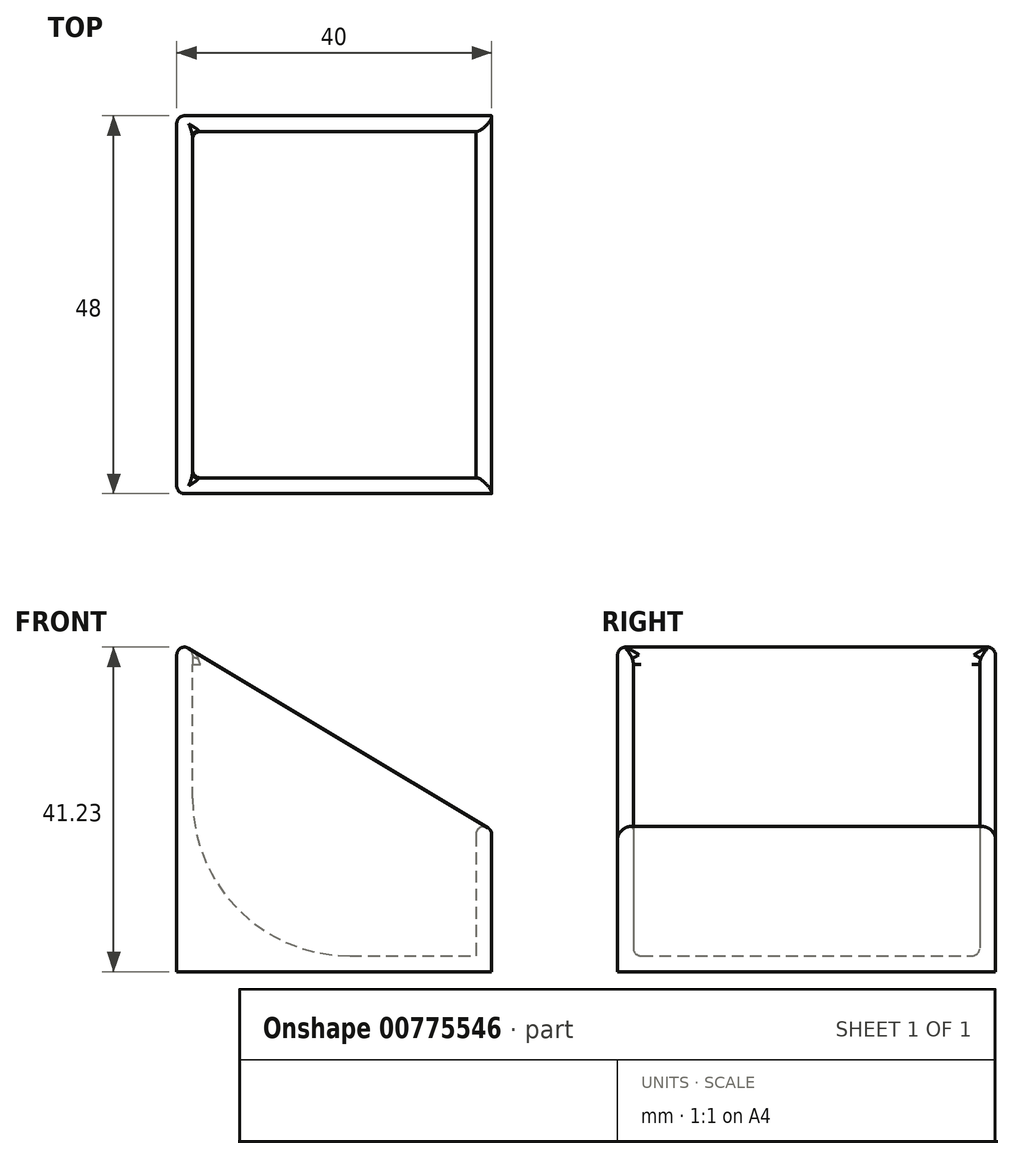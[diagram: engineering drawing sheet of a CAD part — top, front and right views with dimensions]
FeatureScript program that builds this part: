
annotation { "Feature Type Name" : "Feature", "Feature Type Description" : "" }
export const myFeature = defineFeature(function(context is Context, id is Id, definition is map)
    precondition{}
    {
        {
            var Q0;
            Q0=qCreatedBy(makeId("Front.planeOp"),FACE);
            var sketch = newSketch(context, id + "F0", { "sketchPlane" : qUnion([Q0])});
            skLineSegment(sketch, "E0", {"start": v(-20.35, 0) * mm, "end": v(19.65, 0) * mm});
            skLineSegment(sketch, "E1", {"start": v(-20.35, 0) * mm, "end": v(-20.35, 42) * mm});
            skLineSegment(sketch, "E2", {"start": v(-20.35, 42) * mm, "end": v(19.65, 18) * mm});
            skLineSegment(sketch, "E3", {"start": v(19.65, 18) * mm, "end": v(19.65, 0) * mm});
            skSolve(sketch);
        }
        {
            assignVariable(context, id + "F1", {"name" : "Width", "anyValue" : 48});
        }
        {
            var Q0;
            Q0=makeQuery(id+"F0.imprint","IMPRINT",FACE,{"disambiguationData":[TD([[makeQuery(id+"F0.imprint","IMPRINT",EDGE,{"derivedFrom":sQuery(id+"F0.wireOp",EDGE,"E0")}),1.0]])]});
            extrude(context, id + "F2", {"entities" : qUnion([Q0]), "endBound" : BoundingType.SYMMETRIC, "depth" : (getVariable(context, 'Width')) * mm, "offsetDistance" : 25 * mm});
        }
        {
            var Q0;
            Q0=makeQuery(id+"F2.opExtrude","SWEPT_FACE",FACE,{"disambiguationData":[OSD([sQuery(id+"F0.wireOp",EDGE,"E2")])]});
            shell(context, id + "F3", {"entities" : qUnion([Q0]), "thickness" : 2 * mm});
        }
        {
            var Q0;
            Q0=makeQuery(id+"F2.opExtrude","SWEPT_EDGE",EDGE,{"disambiguationData":[OSD([sQuery(id+"F0.wireOp",EDGE,"E1"),sQuery(id+"F0.wireOp",EDGE,"E2")])]});
            var Q1;
            {var subQ0=sQuery(id+"F0.wireOp",EDGE,"E2");Q1=makeQuery(id+"F3.opShell","OFFSET_EDGE",EDGE,{"disambiguationData":[OSD([subQ0]),TDD([makeQuery(id+"F2.opExtrude","CAP_EDGE",EDGE,{"disambiguationData":[OSD([subQ0])],"isStart":false})])]});}
            var Q2;
            {var subQ0=sQuery(id+"F0.wireOp",EDGE,"E2");Q2=makeQuery(id+"F3.opShell","OFFSET_EDGE",EDGE,{"disambiguationData":[OSD([subQ0]),TDD([makeQuery(id+"F2.opExtrude","CAP_EDGE",EDGE,{"disambiguationData":[OSD([subQ0])],"isStart":true})])]});}
            var Q3;
            Q3=makeQuery(id+"F2.opExtrude","CAP_EDGE",EDGE,{"disambiguationData":[OSD([sQuery(id+"F0.wireOp",EDGE,"E2")])],"isStart":true});
            var Q4;
            Q4=makeQuery(id+"F2.opExtrude","CAP_EDGE",EDGE,{"disambiguationData":[OSD([sQuery(id+"F0.wireOp",EDGE,"E2")])],"isStart":false});
            var Q5;
            Q5=makeQuery(id+"F3.opShell","OFFSET_EDGE",EDGE,{"disambiguationData":[OSD([sQuery(id+"F0.wireOp",EDGE,"E1"),sQuery(id+"F0.wireOp",EDGE,"E2")])]});
            var Q6;
            Q6=makeQuery(id+"F3.opShell","OFFSET_EDGE",EDGE,{"disambiguationData":[OSD([sQuery(id+"F0.wireOp",EDGE,"E2"),sQuery(id+"F0.wireOp",EDGE,"E3")])]});
            var Q7;
            Q7=makeQuery(id+"F2.opExtrude","SWEPT_EDGE",EDGE,{"disambiguationData":[OSD([sQuery(id+"F0.wireOp",EDGE,"E2"),sQuery(id+"F0.wireOp",EDGE,"E3")])]});
            fillet(context, id + "F4", {"entities" : qUnion([Q0, Q1, Q2, Q3, Q4, Q5, Q6, Q7]), "radius" : 1 * mm, "tangentPropagation" : true, "allowEdgeOverflow" : false});
        }
        {
            var Q0;
            Q0=makeQuery(id+"F3.opShell","OFFSET_EDGE",EDGE,{"disambiguationData":[OSD([sQuery(id+"F0.wireOp",EDGE,"E0"),sQuery(id+"F0.wireOp",EDGE,"E1")])]});
            fillet(context, id + "F5", {"entities" : qUnion([Q0]), "radius" : 20 * mm, "tangentPropagation" : true, "allowEdgeOverflow" : false});
        }
        {
            var Q0;
            {var subQ0=sQuery(id+"F0.wireOp",EDGE,"E3");var subQ1=sQuery(id+"F0.wireOp",EDGE,"E2");var subQ2=sQuery(id+"F0.wireOp",EDGE,"E1");var subQ3=sQuery(id+"F0.wireOp",EDGE,"E0");Q0=makeQuery(id+"F5.opFillet","BLEND_EDGE",EDGE,{"blendedFrom":[makeQuery(id+"F3.opShell","OFFSET_EDGE",EDGE,{"disambiguationData":[OSD([subQ3,subQ2])]}),makeQuery(id+"F3.opShell","OFFSET_FACE",FACE,{"disambiguationData":[OSD([subQ3,subQ2,subQ1,subQ0]),TDD([makeQuery(id+"F2.opExtrude","CAP_FACE",FACE,{"disambiguationData":[OSD([subQ3,subQ2,subQ1,subQ0])],"isStart":true})])]})],"blendedInto":[makeQuery(id+"F3.opShell","OFFSET_FACE",FACE,{"disambiguationData":[OSD([subQ3,subQ2,subQ1,subQ0]),TDD([makeQuery(id+"F2.opExtrude","CAP_FACE",FACE,{"disambiguationData":[OSD([subQ3,subQ2,subQ1,subQ0])],"isStart":true})])]})]});}
            var Q1;
            {var subQ0=sQuery(id+"F0.wireOp",EDGE,"E1");Q1=makeQuery(id+"F3.opShell","OFFSET_EDGE",EDGE,{"disambiguationData":[OSD([subQ0]),TDD([makeQuery(id+"F2.opExtrude","CAP_EDGE",EDGE,{"disambiguationData":[OSD([subQ0])],"isStart":true})])]});}
            var Q2;
            {var subQ0=sQuery(id+"F0.wireOp",EDGE,"E0");Q2=makeQuery(id+"F3.opShell","OFFSET_EDGE",EDGE,{"disambiguationData":[OSD([subQ0]),TDD([makeQuery(id+"F2.opExtrude","CAP_EDGE",EDGE,{"disambiguationData":[OSD([subQ0])],"isStart":true})])]});}
            var Q3;
            {var subQ0=sQuery(id+"F0.wireOp",EDGE,"E1");Q3=makeQuery(id+"F3.opShell","OFFSET_EDGE",EDGE,{"disambiguationData":[OSD([subQ0]),TDD([makeQuery(id+"F2.opExtrude","CAP_EDGE",EDGE,{"disambiguationData":[OSD([subQ0])],"isStart":false})])]});}
            var Q4;
            {var subQ0=sQuery(id+"F0.wireOp",EDGE,"E3");var subQ1=sQuery(id+"F0.wireOp",EDGE,"E2");var subQ2=sQuery(id+"F0.wireOp",EDGE,"E1");var subQ3=sQuery(id+"F0.wireOp",EDGE,"E0");Q4=makeQuery(id+"F5.opFillet","BLEND_EDGE",EDGE,{"blendedFrom":[makeQuery(id+"F3.opShell","OFFSET_EDGE",EDGE,{"disambiguationData":[OSD([subQ3,subQ2])]}),makeQuery(id+"F3.opShell","OFFSET_FACE",FACE,{"disambiguationData":[OSD([subQ3,subQ2,subQ1,subQ0]),TDD([makeQuery(id+"F2.opExtrude","CAP_FACE",FACE,{"disambiguationData":[OSD([subQ3,subQ2,subQ1,subQ0])],"isStart":false})])]})],"blendedInto":[makeQuery(id+"F3.opShell","OFFSET_FACE",FACE,{"disambiguationData":[OSD([subQ3,subQ2,subQ1,subQ0]),TDD([makeQuery(id+"F2.opExtrude","CAP_FACE",FACE,{"disambiguationData":[OSD([subQ3,subQ2,subQ1,subQ0])],"isStart":false})])]})]});}
            var Q5;
            {var subQ0=sQuery(id+"F0.wireOp",EDGE,"E0");Q5=makeQuery(id+"F3.opShell","OFFSET_EDGE",EDGE,{"disambiguationData":[OSD([subQ0]),TDD([makeQuery(id+"F2.opExtrude","CAP_EDGE",EDGE,{"disambiguationData":[OSD([subQ0])],"isStart":false})])]});}
            fillet(context, id + "F6", {"entities" : qUnion([Q0, Q1, Q2, Q3, Q4, Q5]), "radius" : 1 * mm, "tangentPropagation" : true, "allowEdgeOverflow" : false});
        }
    });
